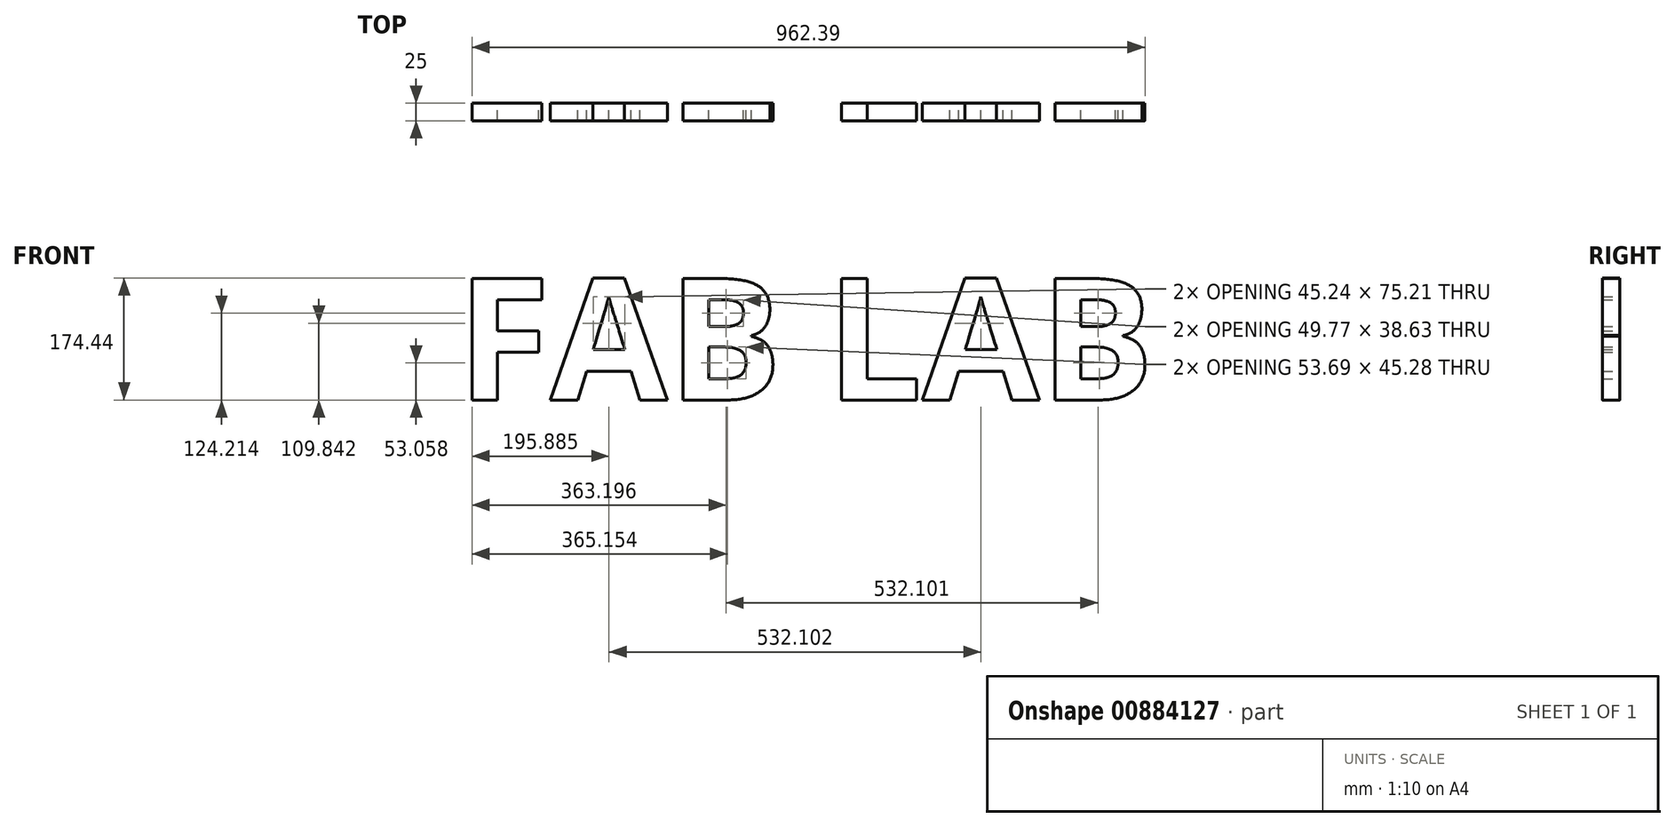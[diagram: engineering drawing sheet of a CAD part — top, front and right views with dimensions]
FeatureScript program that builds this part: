
annotation { "Feature Type Name" : "Feature", "Feature Type Description" : "" }
export const myFeature = defineFeature(function(context is Context, id is Id, definition is map)
    precondition{}
    {
        {
            var Q0;
            Q0=qCreatedBy(makeId("Front.planeOp"),FACE);
            var sketch = newSketch(context, id + "F0", { "sketchPlane" : qUnion([Q0])});
            skText(sketch, "E0", { "text": "FAB LAB ", "fontName": "OpenSans-Bold.ttf"});
            const initialGuessF0  = {"E0": [-0.51267, -0.03329, 1, 0, 0.1752]};
            skSetInitialGuess(sketch, initialGuessF0);
            skSolve(sketch);
        }
        {
            var Q0;
            Q0 = qSketchRegion(id + "F0", true);
            extrude(context, id + "F1", {"entities" : qUnion([Q0]), "depth" : 25 * mm, "offsetDistance" : 25.4 * mm});
        }
    });
